# Revit family: НЕВАТОМ_Решетка РНК_20220407
name_source: partatom
category: Воздухораспределители
revit_build: Autodesk Revit 2017 (Build: 20170118_1100(x64)
units: mm (PartAtom-declared; Revit-internal decimal feet)

## family parameters
Всегда вертикально = Нет
На основе рабочей плоскости = Нет
Общий = Нет
При загрузке вырезать с полостями = Нет
Размер круглого соединителя = Использовать диаметр
Тип детали = Нормальный
Точка расчета площади = Нет

## types (18) — shared parameters
7 = 7 мм
ADSK_Единица измерения = шт
ADSK_Завод-изготовитель = NEVATOM
ADSK_Масса_Текст = кг
ADSK_Материал наименование = Оцинкованння сталь
ADSK_Наименование = РЕШЕТКА РНК-
ADSK_Потеря давления воздуха = 0.0 Па
ADSK_Расход воздуха = 0.0 л/с
Nevatom_URL = https://t.me
t = 2 мм
Материал = Материал корпуса
zero-valued in all types: ADSK_Масса

## per-type parameters (varying)
| type | A | ADSK_Марка | ADSK_Размер_Высота | ADSK_Размер_Длина | ADSK_Размер_Ширина | D | D1 | D2 | Din |
| 100 | 50 мм | 125 | 130 мм | 130 мм | 50 мм | 100 мм | 130 мм | 110 мм | 98 мм |
| 125 | 50 мм | 125 | 155 мм | 155 мм | 50 мм | 125 мм | 155 мм | 135 мм | 123 мм |
| 140 | 50 мм | 140 | 170 мм | 170 мм | 50 мм | 140 мм | 170 мм | 150 мм | 138 мм |
| 800 | 100 мм | 800 | 870 мм | 870 мм | 100 мм | 800 мм | 870 мм | 810 мм | 798 мм |
| 160 | 50 мм | 160 | 190 мм | 190 мм | 50 мм | 160 мм | 190 мм | 170 мм | 158 мм |
| 180 | 50 мм | 180 | 210 мм | 210 мм | 50 мм | 180 мм | 210 мм | 190 мм | 178 мм |
| 200 | 50 мм | 200 | 230 мм | 230 мм | 50 мм | 200 мм | 230 мм | 210 мм | 198 мм |
| 225 | 50 мм | 225 | 255 мм | 255 мм | 50 мм | 225 мм | 255 мм | 235 мм | 223 мм |
| 710 | 70 мм | 710 | 780 мм | 780 мм | 70 мм | 710 мм | 780 мм | 720 мм | 708 мм |
| 630 | 70 мм | 630 | 700 мм | 700 мм | 70 мм | 630 мм | 700 мм | 640 мм | 628 мм |
| 560 | 70 мм | 560 | 630 мм | 630 мм | 70 мм | 560 мм | 630 мм | 570 мм | 558 мм |
| 500 | 70 мм | 500 | 570 мм | 570 мм | 70 мм | 500 мм | 570 мм | 510 мм | 498 мм |
| 450 | 70 мм | 450 | 520 мм | 520 мм | 70 мм | 450 мм | 520 мм | 460 мм | 448 мм |
| 400 | 70 мм | 400 | 470 мм | 470 мм | 70 мм | 400 мм | 470 мм | 410 мм | 398 мм |
| 355 | 70 мм | 355 | 425 мм | 425 мм | 70 мм | 355 мм | 425 мм | 365 мм | 353 мм |
| 315 | 50 мм | 315 | 345 мм | 345 мм | 50 мм | 315 мм | 345 мм | 325 мм | 313 мм |
| 280 | 50 мм | 280 | 310 мм | 310 мм | 50 мм | 280 мм | 310 мм | 290 мм | 278 мм |
| 250 | 50 мм | 250 | 285 мм | 285 мм | 50 мм | 250 мм | 285 мм | 260 мм | 248 мм |
